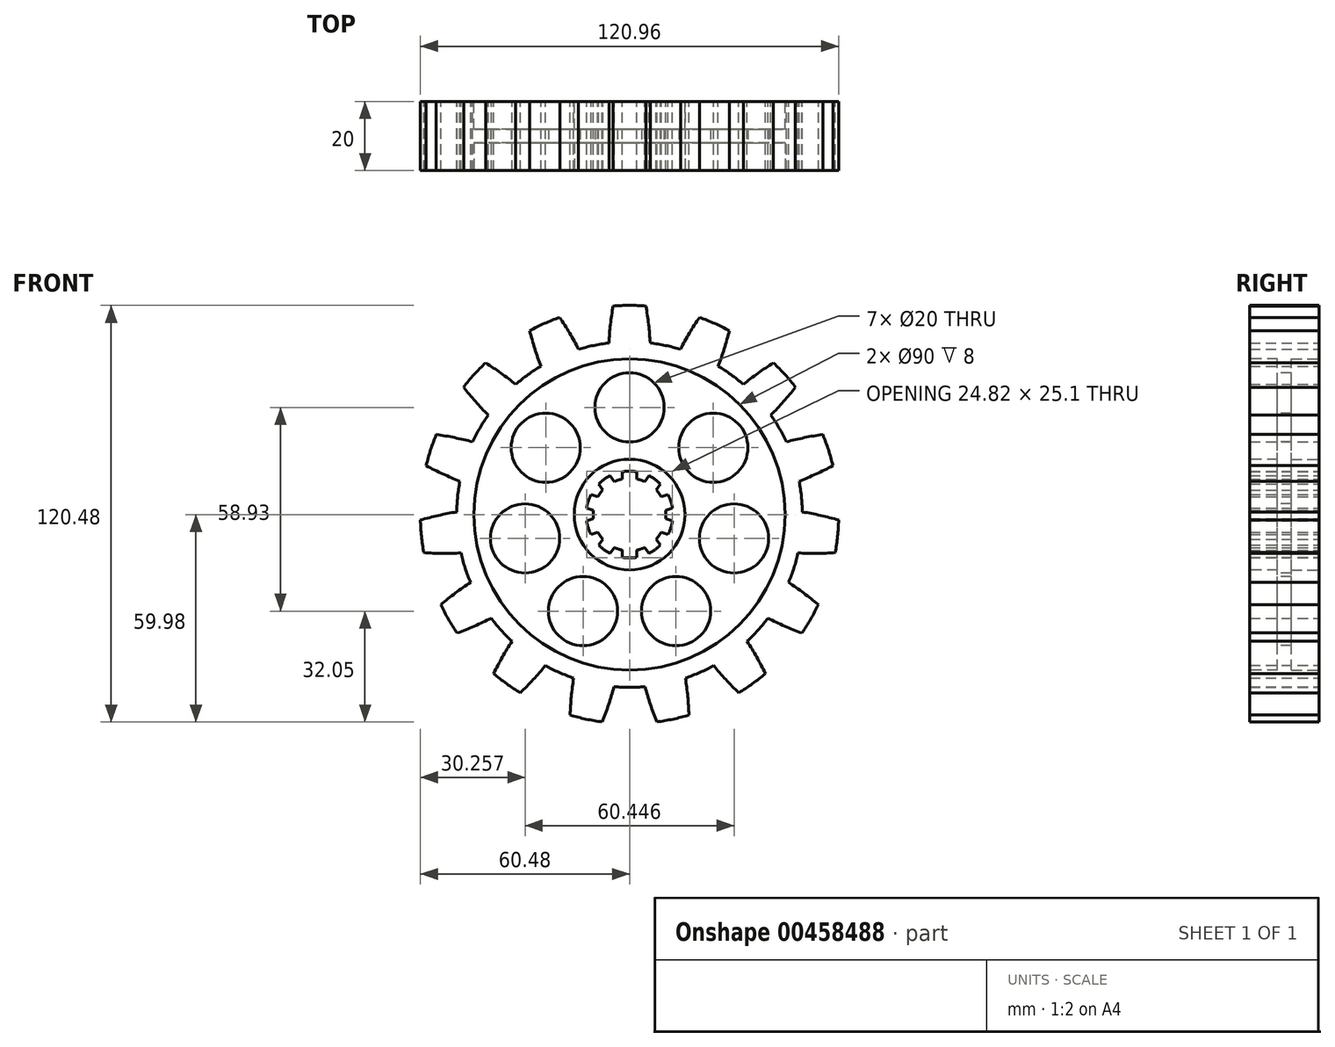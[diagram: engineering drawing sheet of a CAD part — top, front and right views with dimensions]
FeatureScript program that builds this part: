
annotation { "Feature Type Name" : "Feature", "Feature Type Description" : "" }
export const myFeature = defineFeature(function(context is Context, id is Id, definition is map)
    precondition{}
    {
        {
            var Q0;
            Q0=qCreatedBy(makeId("Front.planeOp"),FACE);
            var sketch = newSketch(context, id + "F0", { "sketchPlane" : qUnion([Q0])});
            skCircle(sketch, "E0", {"center": v(0, 0) * mm, "radius": 50 * mm});
            skCircle(sketch, "E1", {"center": v(0, 0) * mm, "radius": 10.5 * mm});
            skLineSegment(sketch, "E2", {"start": v(0, 50) * mm, "end": v(0, 46.5) * mm, "construction": true});
            skLineSegment(sketch, "E3", {"start": v(0, 46.5) * mm, "end": v(83.9, 46.5) * mm, "construction": true});
            skArc(sketch, "E4", {"start": v(-4.75, 60.31) * mm, "mid": v(-5.52, 55) * mm, "end": v(-5.97, 49.64) * mm});
            skArc(sketch, "E5.MirrorC", {"start": v(4.75, 60.31) * mm, "mid": v(5.52, 55) * mm, "end": v(5.97, 49.64) * mm});
            skArc(sketch, "E6.trimOffspring", {"start": v(4.75, 60.31) * mm, "mid": v(0, 60.5) * mm, "end": v(-4.75, 60.31) * mm});
            skArc(sketch, "E7.1.0", {"start": v(-20.2, 57.03) * mm, "mid": v(-24.6, 55.27) * mm, "end": v(-28.87, 53.17) * mm});
            skArc(sketch, "E7.1.1", {"start": v(-28.87, 53.17) * mm, "mid": v(-27.41, 48) * mm, "end": v(-25.64, 42.92) * mm});
            skArc(sketch, "E7.1.2", {"start": v(-20.2, 57.03) * mm, "mid": v(-17.33, 52.49) * mm, "end": v(-14.74, 47.78) * mm});
            skArc(sketch, "E7.2.0", {"start": v(-41.64, 43.89) * mm, "mid": v(-44.96, 40.48) * mm, "end": v(-48, 36.83) * mm});
            skArc(sketch, "E7.2.1", {"start": v(-48, 36.83) * mm, "mid": v(-44.56, 32.7) * mm, "end": v(-40.89, 28.78) * mm});
            skArc(sketch, "E7.2.2", {"start": v(-41.64, 43.89) * mm, "mid": v(-37.18, 40.9) * mm, "end": v(-32.9, 37.65) * mm});
            skArc(sketch, "E7.3.0", {"start": v(-55.9, 23.16) * mm, "mid": v(-57.54, 18.7) * mm, "end": v(-58.83, 14.12) * mm});
            skArc(sketch, "E7.3.1", {"start": v(-58.83, 14.12) * mm, "mid": v(-54, 11.75) * mm, "end": v(-49.06, 9.66) * mm});
            skArc(sketch, "E7.3.2", {"start": v(-55.9, 23.16) * mm, "mid": v(-50.6, 22.24) * mm, "end": v(-45.37, 21.02) * mm});
            skArc(sketch, "E7.4.0", {"start": v(-60.48, -1.58) * mm, "mid": v(-60.17, -6.32) * mm, "end": v(-59.49, -11.03) * mm});
            skArc(sketch, "E7.4.1", {"start": v(-59.49, -11.03) * mm, "mid": v(-54.12, -11.24) * mm, "end": v(-48.75, -11.13) * mm});
            skArc(sketch, "E7.4.2", {"start": v(-60.48, -1.58) * mm, "mid": v(-55.27, -0.26) * mm, "end": v(-50, 0.75) * mm});
            skArc(sketch, "E7.5.0", {"start": v(-54.6, -26.04) * mm, "mid": v(-52.4, -30.25) * mm, "end": v(-49.86, -34.27) * mm});
            skArc(sketch, "E7.5.1", {"start": v(-49.86, -34.27) * mm, "mid": v(-44.87, -32.28) * mm, "end": v(-40, -30) * mm});
            skArc(sketch, "E7.5.2", {"start": v(-54.6, -26.04) * mm, "mid": v(-50.39, -22.72) * mm, "end": v(-45.98, -19.65) * mm});
            skArc(sketch, "E7.6.0", {"start": v(-39.3, -46) * mm, "mid": v(-35.56, -48.95) * mm, "end": v(-31.6, -51.59) * mm});
            skArc(sketch, "E7.6.1", {"start": v(-31.6, -51.59) * mm, "mid": v(-27.86, -47.74) * mm, "end": v(-24.35, -43.67) * mm});
            skArc(sketch, "E7.6.2", {"start": v(-39.3, -46) * mm, "mid": v(-36.8, -41.25) * mm, "end": v(-34, -36.65) * mm});
            skArc(sketch, "E7.7.0", {"start": v(-17.19, -58) * mm, "mid": v(-12.58, -59.18) * mm, "end": v(-7.9, -59.98) * mm});
            skArc(sketch, "E7.7.1", {"start": v(-7.9, -59.98) * mm, "mid": v(-6.04, -54.94) * mm, "end": v(-4.48, -49.8) * mm});
            skArc(sketch, "E7.7.2", {"start": v(-17.19, -58) * mm, "mid": v(-16.83, -52.65) * mm, "end": v(-16.16, -47.32) * mm});
            skArc(sketch, "E7.8.0", {"start": v(7.9, -59.98) * mm, "mid": v(12.58, -59.18) * mm, "end": v(17.19, -58) * mm});
            skArc(sketch, "E7.8.1", {"start": v(17.19, -58) * mm, "mid": v(16.83, -52.65) * mm, "end": v(16.16, -47.32) * mm});
            skArc(sketch, "E7.8.2", {"start": v(7.9, -59.98) * mm, "mid": v(6.04, -54.94) * mm, "end": v(4.48, -49.8) * mm});
            skArc(sketch, "E7.9.0", {"start": v(31.6, -51.59) * mm, "mid": v(35.56, -48.95) * mm, "end": v(39.3, -46) * mm});
            skArc(sketch, "E7.9.1", {"start": v(39.3, -46) * mm, "mid": v(36.8, -41.25) * mm, "end": v(34, -36.65) * mm});
            skArc(sketch, "E7.9.2", {"start": v(31.6, -51.59) * mm, "mid": v(27.86, -47.74) * mm, "end": v(24.35, -43.67) * mm});
            skArc(sketch, "E7.10.0", {"start": v(49.86, -34.27) * mm, "mid": v(52.4, -30.25) * mm, "end": v(54.6, -26.04) * mm});
            skArc(sketch, "E7.10.1", {"start": v(54.6, -26.04) * mm, "mid": v(50.39, -22.72) * mm, "end": v(45.98, -19.65) * mm});
            skArc(sketch, "E7.10.2", {"start": v(49.86, -34.27) * mm, "mid": v(44.87, -32.28) * mm, "end": v(40, -30) * mm});
            skArc(sketch, "E7.11.0", {"start": v(59.49, -11.03) * mm, "mid": v(60.17, -6.32) * mm, "end": v(60.48, -1.58) * mm});
            skArc(sketch, "E7.11.1", {"start": v(60.48, -1.58) * mm, "mid": v(55.27, -0.26) * mm, "end": v(50, 0.75) * mm});
            skArc(sketch, "E7.11.2", {"start": v(59.49, -11.03) * mm, "mid": v(54.12, -11.24) * mm, "end": v(48.75, -11.13) * mm});
            skArc(sketch, "E7.12.0", {"start": v(58.83, 14.12) * mm, "mid": v(57.54, 18.7) * mm, "end": v(55.9, 23.16) * mm});
            skArc(sketch, "E7.12.1", {"start": v(55.9, 23.16) * mm, "mid": v(50.6, 22.24) * mm, "end": v(45.37, 21.02) * mm});
            skArc(sketch, "E7.12.2", {"start": v(58.83, 14.12) * mm, "mid": v(54, 11.75) * mm, "end": v(49.06, 9.66) * mm});
            skArc(sketch, "E7.13.0", {"start": v(48, 36.83) * mm, "mid": v(44.96, 40.48) * mm, "end": v(41.64, 43.89) * mm});
            skArc(sketch, "E7.13.1", {"start": v(41.64, 43.89) * mm, "mid": v(37.18, 40.9) * mm, "end": v(32.9, 37.65) * mm});
            skArc(sketch, "E7.13.2", {"start": v(48, 36.83) * mm, "mid": v(44.56, 32.7) * mm, "end": v(40.89, 28.78) * mm});
            skArc(sketch, "E7.14.0", {"start": v(28.87, 53.17) * mm, "mid": v(24.6, 55.27) * mm, "end": v(20.2, 57.03) * mm});
            skArc(sketch, "E7.14.1", {"start": v(20.2, 57.03) * mm, "mid": v(17.33, 52.49) * mm, "end": v(14.74, 47.78) * mm});
            skArc(sketch, "E7.14.2", {"start": v(28.87, 53.17) * mm, "mid": v(27.41, 48) * mm, "end": v(25.64, 42.92) * mm});
            skSolve(sketch);
        }
        {
            var Q0;
            Q0=makeQuery(id+"F0.imprint","IMPRINT",FACE,{"disambiguationData":[TD([[makeQuery(id+"F0.imprint","IMPRINT",EDGE,{"derivedFrom":sQuery(id+"F0.wireOp",EDGE,"E1")}),-1.0]])]});
            var Q1;
            Q1=makeQuery(id+"F0.imprint","IMPRINT",FACE,{"disambiguationData":[TD([[makeQuery(id+"F0.imprint","IMPRINT",EDGE,{"derivedFrom":sQuery(id+"F0.wireOp",EDGE,"E7.13.0")}),1.0]])]});
            var Q2;
            Q2=makeQuery(id+"F0.imprint","IMPRINT",FACE,{"disambiguationData":[TD([[makeQuery(id+"F0.imprint","IMPRINT",EDGE,{"derivedFrom":sQuery(id+"F0.wireOp",EDGE,"E7.12.0")}),1.0]])]});
            var Q3;
            Q3=makeQuery(id+"F0.imprint","IMPRINT",FACE,{"disambiguationData":[TD([[makeQuery(id+"F0.imprint","IMPRINT",EDGE,{"derivedFrom":sQuery(id+"F0.wireOp",EDGE,"E7.11.0")}),1.0]])]});
            var Q4;
            Q4=makeQuery(id+"F0.imprint","IMPRINT",FACE,{"disambiguationData":[TD([[makeQuery(id+"F0.imprint","IMPRINT",EDGE,{"derivedFrom":sQuery(id+"F0.wireOp",EDGE,"E7.10.0")}),1.0]])]});
            var Q5;
            Q5=makeQuery(id+"F0.imprint","IMPRINT",FACE,{"disambiguationData":[TD([[makeQuery(id+"F0.imprint","IMPRINT",EDGE,{"derivedFrom":sQuery(id+"F0.wireOp",EDGE,"E7.9.0")}),1.0]])]});
            var Q6;
            Q6=makeQuery(id+"F0.imprint","IMPRINT",FACE,{"disambiguationData":[TD([[makeQuery(id+"F0.imprint","IMPRINT",EDGE,{"derivedFrom":sQuery(id+"F0.wireOp",EDGE,"E7.8.0")}),1.0]])]});
            var Q7;
            Q7=makeQuery(id+"F0.imprint","IMPRINT",FACE,{"disambiguationData":[TD([[makeQuery(id+"F0.imprint","IMPRINT",EDGE,{"derivedFrom":sQuery(id+"F0.wireOp",EDGE,"E7.6.0")}),1.0]])]});
            var Q8;
            Q8=makeQuery(id+"F0.imprint","IMPRINT",FACE,{"disambiguationData":[TD([[makeQuery(id+"F0.imprint","IMPRINT",EDGE,{"derivedFrom":sQuery(id+"F0.wireOp",EDGE,"E7.7.0")}),1.0]])]});
            var Q9;
            Q9=makeQuery(id+"F0.imprint","IMPRINT",FACE,{"disambiguationData":[TD([[makeQuery(id+"F0.imprint","IMPRINT",EDGE,{"derivedFrom":sQuery(id+"F0.wireOp",EDGE,"E7.5.0")}),1.0]])]});
            var Q10;
            Q10=makeQuery(id+"F0.imprint","IMPRINT",FACE,{"disambiguationData":[TD([[makeQuery(id+"F0.imprint","IMPRINT",EDGE,{"derivedFrom":sQuery(id+"F0.wireOp",EDGE,"E7.4.0")}),1.0]])]});
            var Q11;
            Q11=makeQuery(id+"F0.imprint","IMPRINT",FACE,{"disambiguationData":[TD([[makeQuery(id+"F0.imprint","IMPRINT",EDGE,{"derivedFrom":sQuery(id+"F0.wireOp",EDGE,"E7.3.0")}),1.0]])]});
            var Q12;
            Q12=makeQuery(id+"F0.imprint","IMPRINT",FACE,{"disambiguationData":[TD([[makeQuery(id+"F0.imprint","IMPRINT",EDGE,{"derivedFrom":sQuery(id+"F0.wireOp",EDGE,"E7.2.0")}),1.0]])]});
            var Q13;
            Q13=makeQuery(id+"F0.imprint","IMPRINT",FACE,{"disambiguationData":[TD([[makeQuery(id+"F0.imprint","IMPRINT",EDGE,{"derivedFrom":sQuery(id+"F0.wireOp",EDGE,"E7.1.0")}),1.0]])]});
            var Q14;
            {var subQ0=sQuery(id+"F0.wireOp",EDGE,"E4");Q14=makeQuery(id+"F0.imprint","IMPRINT",FACE,{"disambiguationData":[TD([[makeQuery(id+"F0.imprint","IMPRINT",EDGE,{"derivedFrom":subQ0}),1.0]])]});}
            var Q15;
            Q15=makeQuery(id+"F0.imprint","IMPRINT",FACE,{"disambiguationData":[TD([[makeQuery(id+"F0.imprint","IMPRINT",EDGE,{"derivedFrom":sQuery(id+"F0.wireOp",EDGE,"E7.14.0")}),1.0]])]});
            extrude(context, id + "F1", {"entities" : qUnion([Q0, Q1, Q2, Q3, Q4, Q5, Q6, Q7, Q8, Q9, Q10, Q11, Q12, Q13, Q14, Q15]), "depth" : 20 * mm});
        }
        {
            var Q0;
            Q0=qCreatedBy(makeId("Front.planeOp"),FACE);
            var sketch = newSketch(context, id + "F2", { "sketchPlane" : qUnion([Q0])});
            skArc(sketch, "E8", {"start": v(2.05, 12.38) * mm, "mid": v(0, 12.55) * mm, "end": v(-2.05, 12.38) * mm});
            skLineSegment(sketch, "E9.left", {"start": v(2.05, 12.38) * mm, "end": v(2.05, -12.38) * mm});
            skLineSegment(sketch, "E9.right", {"start": v(-2.05, 12.38) * mm, "end": v(-2.05, -12.38) * mm});
            skPoint(sketch, "E10.orphan", {"position": v(-2.05, 12.55) * mm});
            skPoint(sketch, "E11.orphan", {"position": v(2.05, 12.55) * mm});
            skPoint(sketch, "E12.orphan", {"position": v(-2.05, -12.55) * mm});
            skPoint(sketch, "E13.orphan", {"position": v(2.05, -12.55) * mm});
            skArc(sketch, "E14.trimOffspring", {"start": v(-2.05, -12.38) * mm, "mid": v(0, -12.55) * mm, "end": v(2.05, -12.38) * mm});
            skArc(sketch, "E15.1.0", {"start": v(-5.62, 11.22) * mm, "mid": v(-7.38, 10.15) * mm, "end": v(-8.94, 8.81) * mm});
            skLineSegment(sketch, "E15.1.1", {"start": v(-5.62, 11.22) * mm, "end": v(8.94, -8.81) * mm});
            skArc(sketch, "E15.2.0", {"start": v(-11.14, 5.78) * mm, "mid": v(-11.94, 3.88) * mm, "end": v(-12.4, 1.88) * mm});
            skLineSegment(sketch, "E15.2.1", {"start": v(-11.14, 5.78) * mm, "end": v(12.4, -1.88) * mm});
            skArc(sketch, "E16.3.3.0", {"start": v(-12.4, -1.88) * mm, "mid": v(-11.94, -3.88) * mm, "end": v(-11.14, -5.78) * mm});
            skLineSegment(sketch, "E16.4.3.0", {"start": v(-12.4, -1.88) * mm, "end": v(11.14, 5.78) * mm});
            skArc(sketch, "E16.3.4.0", {"start": v(-8.94, -8.81) * mm, "mid": v(-7.38, -10.15) * mm, "end": v(-5.62, -11.22) * mm});
            skLineSegment(sketch, "E16.4.4.0", {"start": v(-8.94, -8.81) * mm, "end": v(5.62, 11.22) * mm});
            skLineSegment(sketch, "E16.4.5.0", {"start": v(-2.05, -12.38) * mm, "end": v(-2.05, 12.38) * mm});
            skArc(sketch, "E16.3.6.0", {"start": v(5.62, -11.22) * mm, "mid": v(7.38, -10.15) * mm, "end": v(8.94, -8.81) * mm});
            skLineSegment(sketch, "E16.4.6.0", {"start": v(5.62, -11.22) * mm, "end": v(-8.94, 8.81) * mm});
            skArc(sketch, "E16.3.7.0", {"start": v(11.14, -5.78) * mm, "mid": v(11.94, -3.88) * mm, "end": v(12.4, -1.88) * mm});
            skLineSegment(sketch, "E16.4.7.0", {"start": v(11.14, -5.78) * mm, "end": v(-12.4, 1.88) * mm});
            skArc(sketch, "E16.3.8.0", {"start": v(12.4, 1.88) * mm, "mid": v(11.94, 3.88) * mm, "end": v(11.14, 5.78) * mm});
            skLineSegment(sketch, "E16.4.8.0", {"start": v(12.4, 1.88) * mm, "end": v(-11.14, -5.78) * mm});
            skArc(sketch, "E16.3.9.0", {"start": v(8.94, 8.81) * mm, "mid": v(7.38, 10.15) * mm, "end": v(5.62, 11.22) * mm});
            skLineSegment(sketch, "E16.4.9.0", {"start": v(8.94, 8.81) * mm, "end": v(-5.62, -11.22) * mm});
            skCircle(sketch, "E17", {"center": v(0, 0) * mm, "radius": 10.5 * mm});
            skSolve(sketch);
        }
        {
            var Q0;
            Q0=qSketchRegion(id+"F2",true);
            extrude(context, id + "F3", {"entities" : qUnion([Q0]), "operationType" : NewBodyOperationType.REMOVE, "depth" : 20 * mm});
        }
        {
            var Q0;
            Q0=qCreatedBy(makeId("Front.planeOp"),FACE);
            var sketch = newSketch(context, id + "F4", { "sketchPlane" : qUnion([Q0])});
            skCircle(sketch, "E18", {"center": v(0, 0) * mm, "radius": 16 * mm});
            skCircle(sketch, "E19", {"center": v(0, 0) * mm, "radius": 45 * mm});
            skSolve(sketch);
        }
        {
            var Q0;
            Q0 = qSketchRegion(id + "F4", true);
            extrude(context, id + "F5", {"entities" : qUnion([Q0]), "operationType" : NewBodyOperationType.REMOVE, "depth" : 8 * mm});
        }
        {
            var Q0;
            Q0=makeQuery(id+"F1.opExtrude","CAP_FACE",FACE,{"disambiguationData":[OSD([sQuery(id+"F0.wireOp",EDGE,"E1"),sQuery(id+"F0.wireOp",EDGE,"E4"),sQuery(id+"F0.wireOp",EDGE,"E5.MirrorC"),sQuery(id+"F0.wireOp",EDGE,"E6.trimOffspring"),sQuery(id+"F0.wireOp",EDGE,"E7.1.0"),sQuery(id+"F0.wireOp",EDGE,"E7.1.1"),sQuery(id+"F0.wireOp",EDGE,"E7.1.2"),sQuery(id+"F0.wireOp",EDGE,"E7.2.0"),sQuery(id+"F0.wireOp",EDGE,"E7.2.1"),sQuery(id+"F0.wireOp",EDGE,"E7.2.2"),sQuery(id+"F0.wireOp",EDGE,"E7.3.0"),sQuery(id+"F0.wireOp",EDGE,"E7.3.1"),sQuery(id+"F0.wireOp",EDGE,"E7.3.2"),sQuery(id+"F0.wireOp",EDGE,"E7.4.0"),sQuery(id+"F0.wireOp",EDGE,"E7.4.1"),sQuery(id+"F0.wireOp",EDGE,"E7.4.2"),sQuery(id+"F0.wireOp",EDGE,"E7.5.0"),sQuery(id+"F0.wireOp",EDGE,"E7.5.1"),sQuery(id+"F0.wireOp",EDGE,"E7.5.2"),sQuery(id+"F0.wireOp",EDGE,"E7.6.0"),sQuery(id+"F0.wireOp",EDGE,"E7.6.1"),sQuery(id+"F0.wireOp",EDGE,"E7.6.2"),sQuery(id+"F0.wireOp",EDGE,"E7.7.0"),sQuery(id+"F0.wireOp",EDGE,"E7.7.1"),sQuery(id+"F0.wireOp",EDGE,"E7.7.2"),sQuery(id+"F0.wireOp",EDGE,"E7.8.0"),sQuery(id+"F0.wireOp",EDGE,"E7.8.1"),sQuery(id+"F0.wireOp",EDGE,"E7.8.2"),sQuery(id+"F0.wireOp",EDGE,"E7.9.0"),sQuery(id+"F0.wireOp",EDGE,"E7.9.1"),sQuery(id+"F0.wireOp",EDGE,"E7.9.2"),sQuery(id+"F0.wireOp",EDGE,"E7.10.0"),sQuery(id+"F0.wireOp",EDGE,"E7.10.1"),sQuery(id+"F0.wireOp",EDGE,"E7.10.2"),sQuery(id+"F0.wireOp",EDGE,"E7.11.0"),sQuery(id+"F0.wireOp",EDGE,"E7.11.1"),sQuery(id+"F0.wireOp",EDGE,"E7.11.2"),sQuery(id+"F0.wireOp",EDGE,"E7.12.0"),sQuery(id+"F0.wireOp",EDGE,"E7.12.1"),sQuery(id+"F0.wireOp",EDGE,"E7.12.2"),sQuery(id+"F0.wireOp",EDGE,"E7.13.0"),sQuery(id+"F0.wireOp",EDGE,"E7.13.1"),sQuery(id+"F0.wireOp",EDGE,"E7.13.2"),sQuery(id+"F0.wireOp",EDGE,"E7.14.0"),sQuery(id+"F0.wireOp",EDGE,"E7.14.1"),sQuery(id+"F0.wireOp",EDGE,"E7.14.2"),sQuery(id+"F0.wireOp",EDGE,"E0")])],"isStart":false});
            var Q1;
            Q1 = qBodyType(qCreatedBy(id + "F7" ,EDGE), BodyType.WIRE);
            cPlane(context, id + "F6", {"entities" : qUnion([Q0, Q1]), "cplaneType" : CPlaneType.OFFSET, "offset" : 0 * mm, "width" : 150 * mm, "height" : 150 * mm});
        }
        {
            var Q0;
            Q0=qCreatedBy(id+"F6.planeOp",FACE);
            var sketch = newSketch(context, id + "F7", { "sketchPlane" : qUnion([Q0])});
            skCircle(sketch, "E20", {"center": v(0, 0) * mm, "radius": 16 * mm});
            skCircle(sketch, "E21", {"center": v(0, 0) * mm, "radius": 45 * mm});
            skSolve(sketch);
        }
        {
            var Q0;
            Q0 = qSketchRegion(id + "F7", true);
            var Q1;
            Q1=makeQuery(id+"F7.imprint","IMPRINT",FACE,{"disambiguationData":[TD([[makeQuery(id+"F7.imprint","IMPRINT",EDGE,{"derivedFrom":sQuery(id+"F7.wireOp",EDGE,"E20")}),-1.0]])]});
            extrude(context, id + "F8", {"entities" : qUnion([Q0, Q1]), "operationType" : NewBodyOperationType.REMOVE, "oppositeDirection" : true, "depth" : 8 * mm});
        }
        {
            var Q0;
            Q0=makeQuery(id+"F8.boolean.opBoolean","COPY",FACE,{"derivedFrom":makeQuery(id+"F8.opExtrude","CAP_FACE",FACE,{"disambiguationData":[OSD([sQuery(id+"F7.wireOp",EDGE,"E20"),sQuery(id+"F7.wireOp",EDGE,"E21")])],"isStart":false})});
            cPlane(context, id + "F9", {"entities" : qUnion([Q0]), "cplaneType" : CPlaneType.OFFSET, "offset" : 0 * mm, "width" : 150 * mm, "height" : 150 * mm});
        }
        {
            var Q0;
            Q0=qCreatedBy(id+"F9.planeOp",FACE);
            var sketch = newSketch(context, id + "F10", { "sketchPlane" : qUnion([Q0])});
            skLineSegment(sketch, "E22", {"start": v(0, 0) * mm, "end": v(0, 31) * mm, "construction": true});
            skCircle(sketch, "E23", {"center": v(0, 31) * mm, "radius": 10 * mm});
            skCircle(sketch, "E24.1.0", {"center": v(-24.24, 19.33) * mm, "radius": 10 * mm});
            skCircle(sketch, "E24.2.0", {"center": v(-30.22, -6.9) * mm, "radius": 10 * mm});
            skCircle(sketch, "E24.3.0", {"center": v(-13.45, -27.93) * mm, "radius": 10 * mm});
            skCircle(sketch, "E24.4.0", {"center": v(13.45, -27.93) * mm, "radius": 10 * mm});
            skCircle(sketch, "E24.5.0", {"center": v(30.22, -6.9) * mm, "radius": 10 * mm});
            skCircle(sketch, "E24.6.0", {"center": v(24.24, 19.33) * mm, "radius": 10 * mm});
            skPoint(sketch, "E24.center", {"position": v(0, 0) * mm});
            skSolve(sketch);
        }
        {
            var Q0;
            Q0=makeQuery(id+"F10.imprint","IMPRINT",FACE,{"disambiguationData":[TD([[makeQuery(id+"F10.imprint","IMPRINT",EDGE,{"derivedFrom":sQuery(id+"F10.wireOp",EDGE,"E24.1.0")}),1.0]])]});
            var Q1;
            Q1=makeQuery(id+"F10.imprint","IMPRINT",FACE,{"disambiguationData":[TD([[makeQuery(id+"F10.imprint","IMPRINT",EDGE,{"derivedFrom":sQuery(id+"F10.wireOp",EDGE,"E23")}),1.0]])]});
            var Q2;
            Q2=makeQuery(id+"F10.imprint","IMPRINT",FACE,{"disambiguationData":[TD([[makeQuery(id+"F10.imprint","IMPRINT",EDGE,{"derivedFrom":sQuery(id+"F10.wireOp",EDGE,"E24.6.0")}),1.0]])]});
            var Q3;
            Q3=makeQuery(id+"F10.imprint","IMPRINT",FACE,{"disambiguationData":[TD([[makeQuery(id+"F10.imprint","IMPRINT",EDGE,{"derivedFrom":sQuery(id+"F10.wireOp",EDGE,"E24.5.0")}),1.0]])]});
            var Q4;
            Q4=makeQuery(id+"F10.imprint","IMPRINT",FACE,{"disambiguationData":[TD([[makeQuery(id+"F10.imprint","IMPRINT",EDGE,{"derivedFrom":sQuery(id+"F10.wireOp",EDGE,"E24.3.0")}),1.0]])]});
            var Q5;
            Q5=makeQuery(id+"F10.imprint","IMPRINT",FACE,{"disambiguationData":[TD([[makeQuery(id+"F10.imprint","IMPRINT",EDGE,{"derivedFrom":sQuery(id+"F10.wireOp",EDGE,"E24.2.0")}),1.0]])]});
            var Q6;
            Q6=makeQuery(id+"F10.imprint","IMPRINT",FACE,{"disambiguationData":[TD([[makeQuery(id+"F10.imprint","IMPRINT",EDGE,{"derivedFrom":sQuery(id+"F10.wireOp",EDGE,"E24.4.0")}),1.0]])]});
            extrude(context, id + "F11", {"entities" : qUnion([Q0, Q1, Q2, Q3, Q4, Q5, Q6]), "operationType" : NewBodyOperationType.REMOVE, "oppositeDirection" : true, "depth" : 25 * mm});
        }
    });
